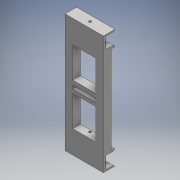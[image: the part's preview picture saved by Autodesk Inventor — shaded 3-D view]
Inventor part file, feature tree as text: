
AUTODESK INVENTOR PART (.ipt)
format: ipt  version: 2016 (Build 200138000, 138)  size: 217,600 bytes
history: native  units: mm
features: extrude x7, sketch x7, chamfer x3
ambient origin geometry x8: Origin, YZ Plane, XZ Plane, XY Plane, X Axis, Y Axis, Z Axis, Center Point
bodies: Solid1 (feature_tree)
feature tree (17):
  extrude  "Extrusion1"  Depth=155.0mm
  extrude  "Extrusion2"  Depth=10.0mm
  extrude  "Extrusion3"  Depth=5.0mm TaperAngle=0.0deg
  extrude  "Extrusion4"  Depth=10.0mm
  extrude  "Extrusion5"  Depth=10.0mm
  chamfer  "Chamfer1"  Distance=5.0mm
  chamfer  "Chamfer2"  Distance=50.0mm
  chamfer  "Chamfer3"  Distance=10.0mm
  extrude  "Extrusion6"  Depth=10.0mm
  extrude  "Extrusion7"  Depth=10.0mm
  sketch  "Sketch1"  dims[d0=50.0mm d1=155.0mm]
  sketch  "Sketch2"  dims[d2=10.0mm d3=0.0mm d4=20.0mm]
  sketch  "Sketch3"  dims[d5=20.0mm d6=5.0mm d7=0.0mm]
  sketch  "Sketch4"  dims[d8=5.0mm d9=10.0mm]
  sketch  "Sketch5"  dims[d10=5.0mm d11=10.0mm d12=5.0mm d13=0.0mm d15=50.0mm d16=0.0mm]
  sketch  "Sketch6"  dims[d17=10.0mm]
  sketch  "Sketch7"  dims[d18=10.0mm d19=10.0mm d21=10.0mm d22=2.5mm d23=5.0mm d24=5.0mm d25=5.0mm d26=10.0mm d27=0.0mm d28=7.0mm d29=2.0mm d30=45.0deg d31=5.0mm d32=2.0mm d33=45.0deg d34=3.0mm d35=2.0mm d36=45.0deg d37=3.0mm d38=40.0mm d39=0.0mm d40=30.0mm d41=0.0mm d44=5.0mm]
